# Revit family: FP-Revit19-en-CI122DB1-CI152DB1-CI152DTTB1-CI244DTTB1-CI304DTTB1-CI365DTTB1-InductionCooktop-0-90003220A-US-CA
name_source: partatom
category: Specialty Equipment
units: mm (PartAtom-declared; Revit-internal decimal feet)

## family parameters
Always vertical = Yes
Cut with Voids When Loaded = Yes
OmniClass Number = 23.40.40.14.17.11
OmniClass Title = Cookers, Ovens, Stoves
Part Type = Normal
Room Calculation Point = No
Round Connector Dimension = Use Diameter
Shared = No
Work Plane-Based = No

## types (6) — shared parameters
Cavity - Depth (Flush Mount) = 509 mm
Cavity - Depth (Proud Mount) = 507 mm
Chassis - Depth = 504 mm
Chassis - Height = 56 mm  [stored 0.183727 ft]
Clearance - Overhead Non-Combustible = 450 mm  [stored 1.47638 ft]
Clearance - Overhead Rangehood = 650 mm  [stored 2.13255 ft]
Clearance - Rear Combustible = 20 mm  [stored 0.0656168 ft]
Clearance - Side Combustible = 27 mm  [stored 0.0885827 ft]
Manufacturer = Fisher & Paykel Appliances Ltd
Material - Body = Fisher & Paykel - Grey
Material - Cooktop = Fisher & Paykel - Glass, Black
Material - Display Panel = Fisher & Paykel - Grey, Charcoal
Material - Graphics = Fisher & Paykel - Grey, Charcoal
Product - Depth = 530 mm  [stored 1.73885 ft]
Product - Height = 62 mm  [stored 0.203412 ft]
Recess - Depth = 7 mm  [stored 0.0229659 ft]
Visibility - Clearance Required = Yes
Visibility - Power Flex Large = No

## per-type parameters (varying)
| type | Cavity - Height | Cavity - Width | Chassis - Width | Connector Description - Electrical | Description | Graphics - 30/15 | Graphics - 39/17 | Graphics - 60/24 | Graphics - 76/30 | Graphics - 90/36 | Product - Width | Visibility - Power Conduit US-CA | Visibility - Power Flex Small | Visibility - Touchscreen |
| CI122DB1 | 72 mm  [stored 0.23622 ft] | 262 mm  [stored 0.85958 ft] | 254 mm  [stored 0.833333 ft] | 120V, 60Hz, 20A | 12", 2 Zone Induction Cooktop, Black | Yes | No | No | No | No | 300 mm | No | Yes | No |
| CI152DTTB1 | 72 mm  [stored 0.23622 ft] | 347 mm | 334 mm | 120V, 60Hz, 20A | 15", 2 Zone Induction Cooktop, Black, Touchscreen | No | Yes | No | No | No | 385 mm | No | Yes | Yes |
| CI244DTTB1 | 95 mm | 562 mm | 554 mm | 120V, 60Hz, 35A | 24", 4 Zone Induction Cooktop, Black, Touchscreen | No | No | Yes | No | No | 600 mm | Yes | No | Yes |
| CI304DTTB1 | 95 mm | 722 mm | 714 mm | 120V, 60Hz, 35A | 30", 4 Zone Induction Cooktop, Black, Touchscreen | No | No | No | Yes | No | 760 mm | Yes | No | Yes |
| CI365DTTB1 | 95 mm | 862 mm | 854 mm | 120V, 60Hz, 50A | 36", 5 Zone Induction Cooktop, Black, Touchscreen | No | No | No | No | Yes | 900 mm  [stored 2.95276 ft] | Yes | No | Yes |
| CI152DB1 | 72 mm  [stored 0.23622 ft] | 347 mm | 334 mm | 120V, 60Hz, 20A | 15", 2 Zone Induction Cooktop, Black | No | Yes | No | No | No | 385 mm | No | Yes | No |

note: column(s) folded — value = type name in every type: Model

note: [stored X ft] marks values corroborated as IEEE doubles in the binary element streams (Revit-internal decimal feet)

## geometry (parser evidence)
native form markers: Sweep x6
no freeform markers — native parametric forms only
